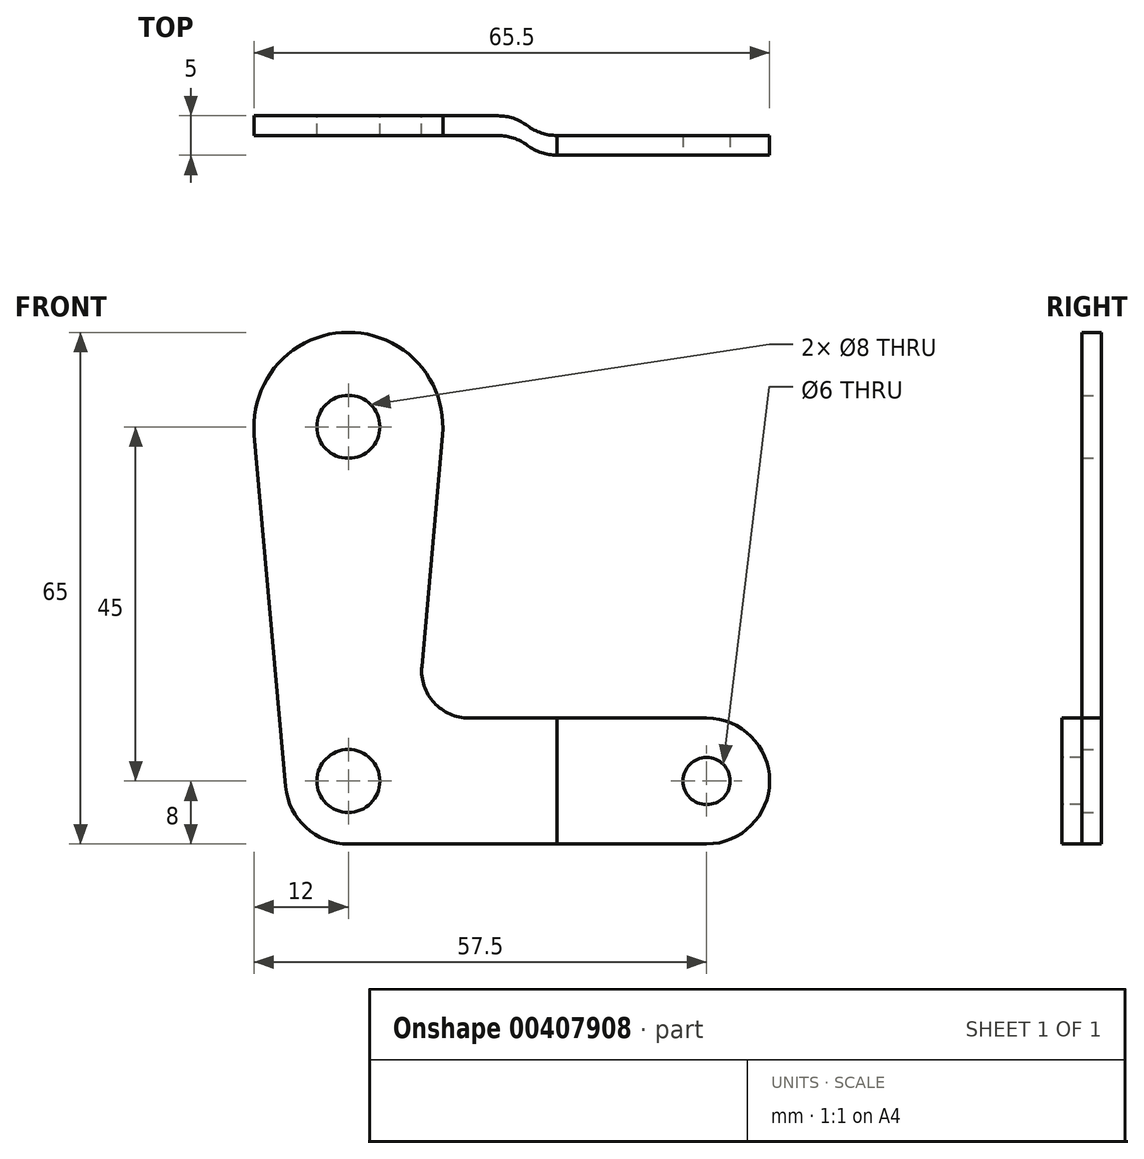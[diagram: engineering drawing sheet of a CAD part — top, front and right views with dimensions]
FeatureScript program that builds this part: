
annotation { "Feature Type Name" : "Feature", "Feature Type Description" : "" }
export const myFeature = defineFeature(function(context is Context, id is Id, definition is map)
    precondition{}
    {
        {
            var Q0;
            Q0=qCreatedBy(makeId("Front.planeOp"),FACE);
            var sketch = newSketch(context, id + "F0", { "sketchPlane" : qUnion([Q0])});
            skCircle(sketch, "E0", {"center": v(0, 0) * mm, "radius": 4 * mm});
            skCircle(sketch, "E1", {"center": v(0, 45) * mm, "radius": 4 * mm});
            skArc(sketch, "E2", {"start": v(0, -8) * mm, "mid": v(-5.4, -5.9) * mm, "end": v(-7.97, -0.71) * mm});
            skArc(sketch, "E3", {"start": v(11.95, 43.93) * mm, "mid": v(0, 57) * mm, "end": v(-11.95, 43.93) * mm});
            skLineSegment(sketch, "E4", {"start": v(-11.95, 43.93) * mm, "end": v(-7.97, -0.71) * mm});
            skLineSegment(sketch, "E5", {"start": v(11.95, 43.93) * mm, "end": v(9.33, 14.53) * mm});
            skArc(sketch, "E6", {"start": v(9.33, 14.53) * mm, "mid": v(10.88, 9.95) * mm, "end": v(15.3, 8) * mm});
            skLineSegment(sketch, "E7", {"start": v(15.3, 8) * mm, "end": v(19, 8) * mm});
            skLineSegment(sketch, "E8", {"start": v(0, -8) * mm, "end": v(19, -8) * mm});
            skLineSegment(sketch, "E9", {"start": v(19, 8) * mm, "end": v(19, -8) * mm});
            skSolve(sketch);
        }
        {
            var Q0;
            Q0=makeQuery(id+"F0.imprint","IMPRINT",FACE,{"disambiguationData":[TD([[makeQuery(id+"F0.imprint","IMPRINT",EDGE,{"derivedFrom":sQuery(id+"F0.wireOp",EDGE,"E0")}),-1.0]])]});
            extrude(context, id + "F1", {"entities" : qUnion([Q0]), "depth" : 2.5 * mm});
        }
        {
            var Q0;
            Q0=qCreatedBy(makeId("Top.planeOp"),FACE);
            var sketch = newSketch(context, id + "F2", { "sketchPlane" : qUnion([Q0])});
            skPoint(sketch, "E10.0", {"position": v(19, -2.5) * mm});
            skPoint(sketch, "E11.0", {"position": v(19, 0) * mm});
            skLineSegment(sketch, "E12.0", {"start": v(19, -2.5) * mm, "end": v(19, 0) * mm});
            skLineSegment(sketch, "E13", {"start": v(26.5, -2.5) * mm, "end": v(26.5, -5) * mm});
            skArc(sketch, "E14", {"start": v(22.75, -1.25) * mm, "mid": v(20.98, -0.32) * mm, "end": v(19, 0) * mm});
            skArc(sketch, "E15", {"start": v(22.75, -1.25) * mm, "mid": v(24.52, -2.18) * mm, "end": v(26.5, -2.5) * mm});
            skArc(sketch, "E16", {"start": v(22.75, -3.75) * mm, "mid": v(20.98, -2.82) * mm, "end": v(19, -2.5) * mm});
            skArc(sketch, "E17", {"start": v(22.75, -3.75) * mm, "mid": v(24.52, -4.68) * mm, "end": v(26.5, -5) * mm});
            skSolve(sketch);
        }
        {
            var Q0;
            Q0=makeQuery(id+"F2.imprint","IMPRINT",FACE,{"disambiguationData":[TD([[makeQuery(id+"F2.imprint","IMPRINT",EDGE,{"derivedFrom":sQuery(id+"F2.wireOp",EDGE,"E12.0")}),-1.0]])]});
            extrude(context, id + "F3", {"entities" : qUnion([Q0]), "operationType" : NewBodyOperationType.ADD, "endBound" : BoundingType.SYMMETRIC, "depth" : 16 * mm});
        }
        {
            var Q0;
            Q0=makeQuery(id+"F1.opExtrude","CAP_FACE",FACE,{"disambiguationData":[OSD([sQuery(id+"F0.wireOp",EDGE,"E0"),sQuery(id+"F0.wireOp",EDGE,"E1"),sQuery(id+"F0.wireOp",EDGE,"E2"),sQuery(id+"F0.wireOp",EDGE,"E3"),sQuery(id+"F0.wireOp",EDGE,"E4"),sQuery(id+"F0.wireOp",EDGE,"E5"),sQuery(id+"F0.wireOp",EDGE,"E6"),sQuery(id+"F0.wireOp",EDGE,"E7"),sQuery(id+"F0.wireOp",EDGE,"E8"),sQuery(id+"F0.wireOp",EDGE,"E9")])],"isStart":false});
            cPlane(context, id + "F4", {"entities" : qUnion([Q0]), "cplaneType" : CPlaneType.OFFSET, "offset" : 2.5 * mm, "width" : 150 * mm, "height" : 150 * mm});
        }
        {
            var Q0;
            Q0=qCreatedBy(id+"F4.planeOp",FACE);
            var sketch = newSketch(context, id + "F5", { "sketchPlane" : qUnion([Q0])});
            skPoint(sketch, "E18.0", {"position": v(26.5, 8) * mm});
            skPoint(sketch, "E19.0", {"position": v(26.5, -8) * mm});
            skLineSegment(sketch, "E20.0", {"start": v(26.5, 8) * mm, "end": v(26.5, -8) * mm});
            skLineSegment(sketch, "E21", {"start": v(26.5, -8) * mm, "end": v(45.5, -8) * mm});
            skLineSegment(sketch, "E22", {"start": v(26.5, 8) * mm, "end": v(45.5, 8) * mm});
            skArc(sketch, "E23", {"start": v(45.5, -8) * mm, "mid": v(53.5, 0) * mm, "end": v(45.5, 8) * mm});
            skCircle(sketch, "E24", {"center": v(45.5, 0) * mm, "radius": 3 * mm});
            skSolve(sketch);
        }
        {
            var Q0;
            Q0=makeQuery(id+"F5.imprint","IMPRINT",FACE,{"disambiguationData":[TD([[makeQuery(id+"F5.imprint","IMPRINT",EDGE,{"derivedFrom":sQuery(id+"F5.wireOp",EDGE,"E20.0")}),1.0]])]});
            extrude(context, id + "F6", {"entities" : qUnion([Q0]), "oppositeDirection" : true, "depth" : 2.5 * mm});
        }
    });
